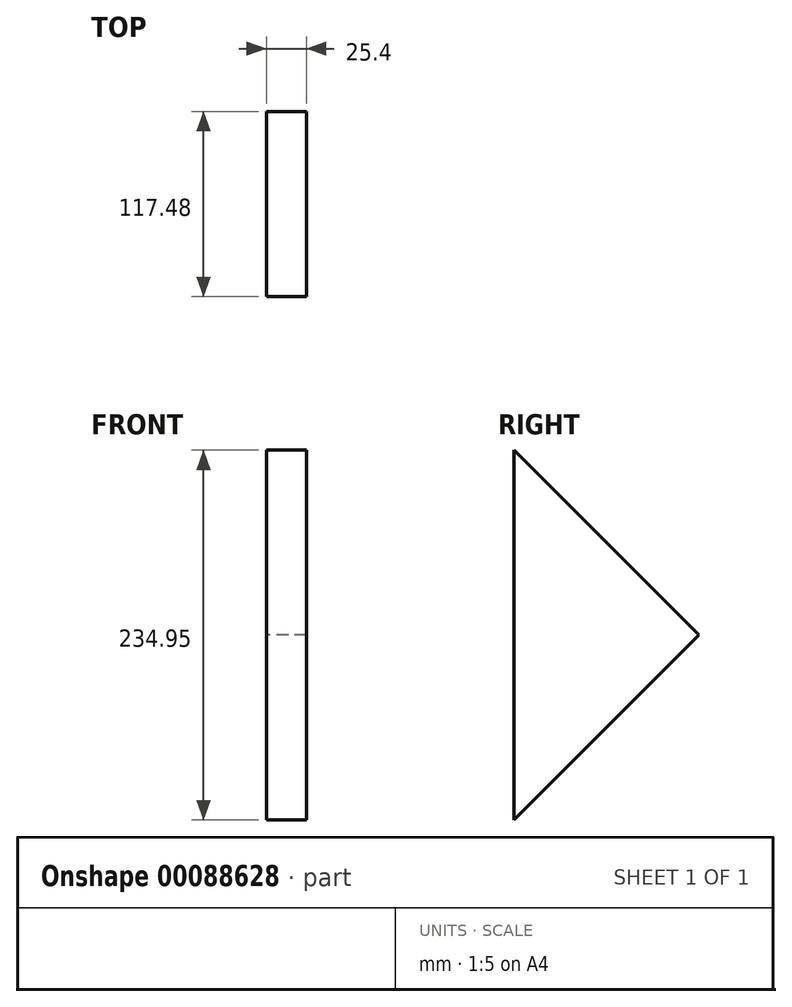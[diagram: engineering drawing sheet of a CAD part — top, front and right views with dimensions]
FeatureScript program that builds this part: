
annotation { "Feature Type Name" : "Feature", "Feature Type Description" : "" }
export const myFeature = defineFeature(function(context is Context, id is Id, definition is map)
    precondition{}
    {
        {
            var Q0;
            Q0=qCreatedBy(makeId("Right.planeOp"),FACE);
            var sketch = newSketch(context, id + "F0", { "sketchPlane" : qUnion([Q0])});
            skLineSegment(sketch, "E0", {"start": v(-156.64, 166.37) * mm, "end": v(78.31, 166.37) * mm});
            skLineSegment(sketch, "E1", {"start": v(-156.64, 166.37) * mm, "end": v(-156.64, -68.58) * mm});
            skLineSegment(sketch, "E2", {"start": v(-156.64, -68.58) * mm, "end": v(78.31, -68.58) * mm});
            skLineSegment(sketch, "E3", {"start": v(78.31, -68.58) * mm, "end": v(78.31, 166.37) * mm});
            skLineSegment(sketch, "E4", {"start": v(-156.64, 166.37) * mm, "end": v(78.31, -68.58) * mm});
            skLineSegment(sketch, "E5", {"start": v(-156.64, -68.58) * mm, "end": v(78.31, 166.37) * mm});
            skSolve(sketch);
        }
        {
            var Q0;
            {var subQ0=sQuery(id+"F0.wireOp",EDGE,"E1");Q0=makeQuery(id+"F0.imprint","IMPRINT",FACE,{"disambiguationData":[TD([[makeQuery(id+"F0.imprint","IMPRINT",EDGE,{"derivedFrom":subQ0}),1.0]])]});}
            extrude(context, id + "F1", {"entities" : qUnion([Q0]), "depth" : 25.4 * mm});
        }
    });
